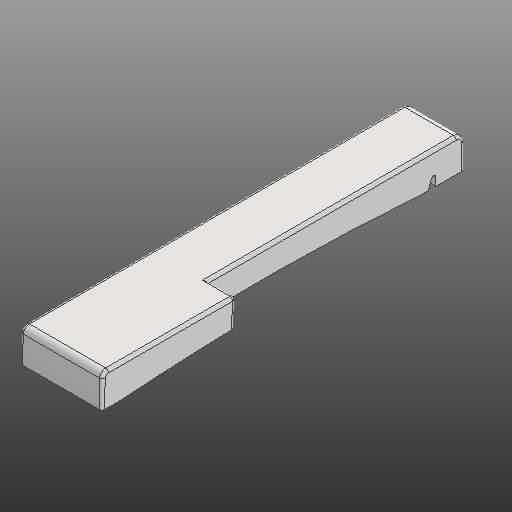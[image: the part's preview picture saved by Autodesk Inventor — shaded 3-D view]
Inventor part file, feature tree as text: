
AUTODESK INVENTOR PART (.ipt)
format: ipt  version: 2020 (Build 240168000, 168)  size: 324,608 bytes
history: native  units: in
note: dims shown in document units (in); Inventor stores cm internally (conversion verified against a paired STEP export)
features: extrude x4, other x3, fillet x2
ambient origin geometry x8: Origin, YZ Plane, XZ Plane, XY Plane, X Axis, Y Axis, Z Axis, Center Point
bodies: Solid1 (feature_tree)
feature tree (9):
  other  "Slot Start Plane"
  other  "Key Profile"
  extrude  "Upper (u)"  TaperAngle=0.0deg  [1 undecoded]
  extrude  "Lower (d)"  TaperAngle=0.0deg  [1 undecoded]
  extrude  "Protrusion Cutout"  Depth=0.0591in
  fillet  "Front Fillet"  Radius=0.1374in
  extrude  "Slot"  [1 undecoded]
  fillet  "Edge Softening"  Radius=0.0787in
  other  "Slot Sketch"
note: 3 required parameter values undecoded (feature->parameter linkage not recoverable at this tier; creation-order binding heuristic only, values carry confidence <= 0.55)
